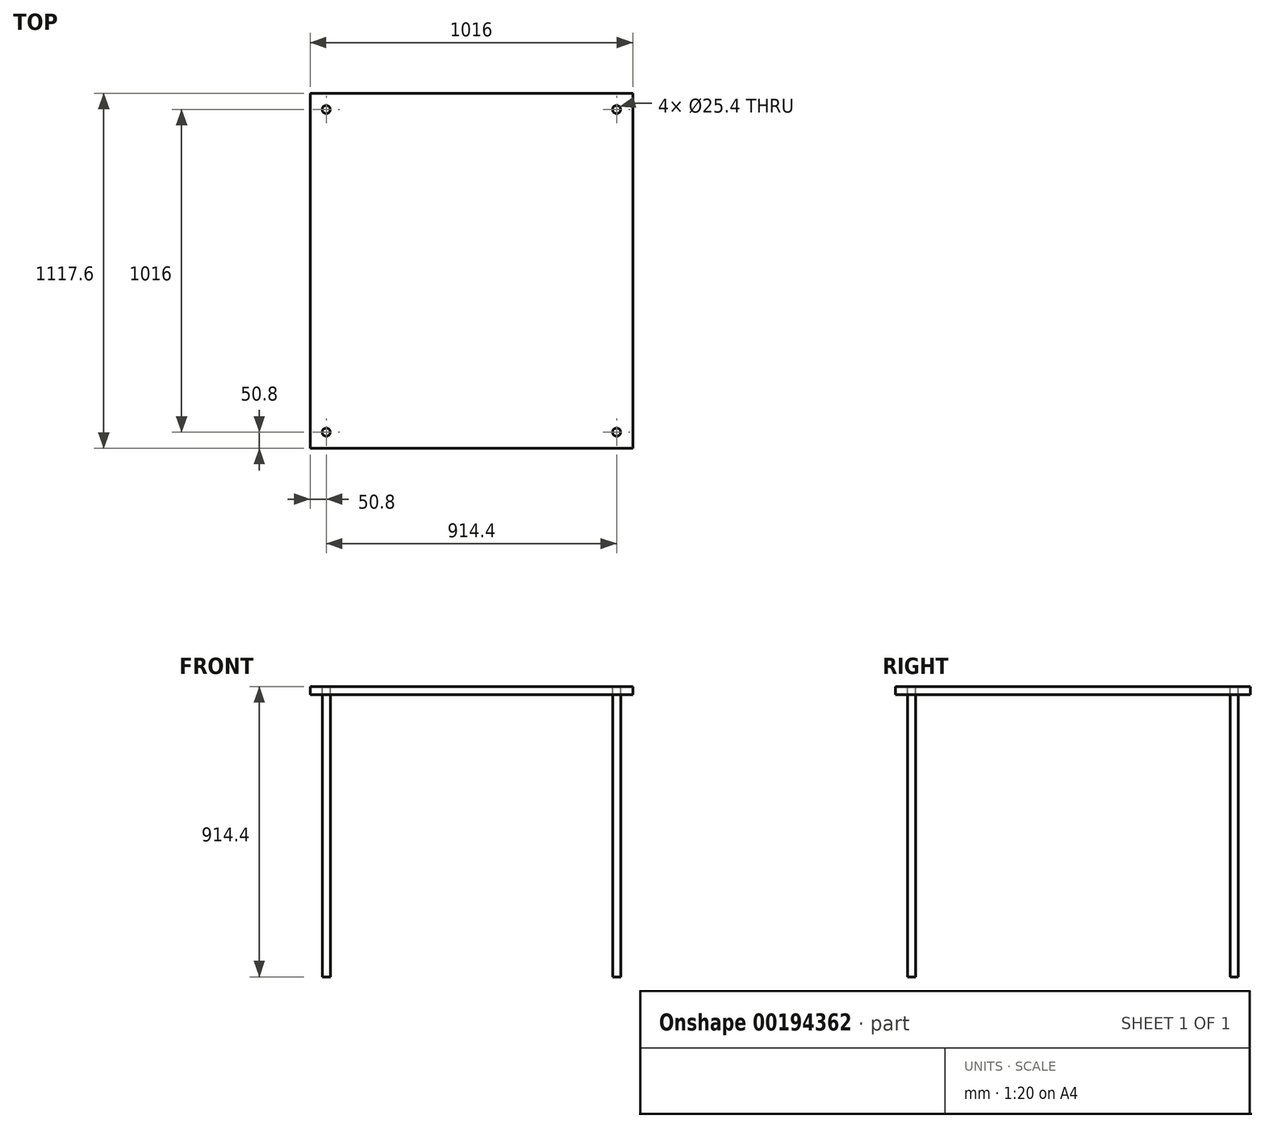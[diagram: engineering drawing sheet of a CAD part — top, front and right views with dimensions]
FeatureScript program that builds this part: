
annotation { "Feature Type Name" : "Feature", "Feature Type Description" : "" }
export const myFeature = defineFeature(function(context is Context, id is Id, definition is map)
    precondition{}
    {
        {
            var Q0;
            Q0=qCreatedBy(makeId("Top.planeOp"),FACE);
            var sketch = newSketch(context, id + "F0", { "sketchPlane" : qUnion([Q0])});
            skLineSegment(sketch, "E0.bottom", {"start": v(508, 558.8) * mm, "end": v(-508, 558.8) * mm});
            skLineSegment(sketch, "E0.top", {"start": v(508, -558.8) * mm, "end": v(-508, -558.8) * mm});
            skLineSegment(sketch, "E0.left", {"start": v(508, 558.8) * mm, "end": v(508, -558.8) * mm});
            skLineSegment(sketch, "E0.right", {"start": v(-508, 558.8) * mm, "end": v(-508, -558.8) * mm});
            skPoint(sketch, "E0.middle", {"position": v(0, 0) * mm});
            skLineSegment(sketch, "E1.bottom", {"start": v(457.2, 508) * mm, "end": v(-457.2, 508) * mm});
            skLineSegment(sketch, "E1.top", {"start": v(457.2, -508) * mm, "end": v(-457.2, -508) * mm});
            skLineSegment(sketch, "E1.left", {"start": v(457.2, 508) * mm, "end": v(457.2, -508) * mm});
            skLineSegment(sketch, "E1.right", {"start": v(-457.2, 508) * mm, "end": v(-457.2, -508) * mm});
            skCircle(sketch, "E2", {"center": v(-457.2, -508) * mm, "radius": 12.7 * mm});
            skCircle(sketch, "E3", {"center": v(457.2, -508) * mm, "radius": 12.7 * mm});
            skCircle(sketch, "E4", {"center": v(-457.2, 508) * mm, "radius": 12.7 * mm});
            skCircle(sketch, "E5", {"center": v(457.2, 508) * mm, "radius": 12.7 * mm});
            skSolve(sketch);
        }
        {
            var Q0;
            Q0=makeQuery(id+"F0.imprint","IMPRINT",FACE,{"disambiguationData":[TD([[makeQuery(id+"F0.imprint","IMPRINT",EDGE,{"derivedFrom":sQuery(id+"F0.wireOp",EDGE,"E0.bottom")}),1.0]])]});
            var Q1;
            {var subQ10=sQuery(id+"F0.wireOp",EDGE,"E5");var subQ13=sQuery(id+"F0.wireOp",EDGE,"E1.bottom");var subQ15=makeQuery(id+"F0.imprint","INTERSECT",VERTEX,{"derivedFrom":[subQ13,subQ10]});Q1=makeQuery(id+"F0.imprint","IMPRINT",FACE,{"disambiguationData":[TD([[makeQuery(id+"F0.imprint","IMPRINT",EDGE,{"disambiguationData":[TD([[subQ15,-1.0]])],"derivedFrom":subQ13}),1.0]])]});}
            extrude(context, id + "F1", {"entities" : qUnion([Q0, Q1]), "oppositeDirection" : true, "depth" : 25.4 * mm});
        }
        {
            var Q0;
            {var subQ0=sQuery(id+"F0.wireOp",EDGE,"E1.right");var subQ1=sQuery(id+"F0.wireOp",EDGE,"E1.top");var subQ2=makeQuery(id+"F0.imprint","INTERSECT",VERTEX,{"derivedFrom":[subQ1,subQ0]});Q0=makeQuery(id+"F0.imprint","IMPRINT",FACE,{"disambiguationData":[TD([[makeQuery(id+"F0.imprint","IMPRINT",EDGE,{"disambiguationData":[TD([[subQ2,1.0]])],"derivedFrom":subQ1}),1.0]])]});}
            var Q1;
            {var subQ0=sQuery(id+"F0.wireOp",EDGE,"E1.right");var subQ1=sQuery(id+"F0.wireOp",EDGE,"E1.top");var subQ2=makeQuery(id+"F0.imprint","INTERSECT",VERTEX,{"derivedFrom":[subQ1,subQ0]});Q1=makeQuery(id+"F0.imprint","IMPRINT",FACE,{"disambiguationData":[TD([[makeQuery(id+"F0.imprint","IMPRINT",EDGE,{"disambiguationData":[TD([[subQ2,1.0]])],"derivedFrom":subQ1}),-1.0]])]});}
            var Q2;
            {var subQ0=sQuery(id+"F0.wireOp",EDGE,"E1.left");var subQ1=sQuery(id+"F0.wireOp",EDGE,"E1.top");var subQ2=makeQuery(id+"F0.imprint","INTERSECT",VERTEX,{"derivedFrom":[subQ1,subQ0]});Q2=makeQuery(id+"F0.imprint","IMPRINT",FACE,{"disambiguationData":[TD([[makeQuery(id+"F0.imprint","IMPRINT",EDGE,{"disambiguationData":[TD([[subQ2,-1.0]])],"derivedFrom":subQ1}),1.0]])]});}
            var Q3;
            {var subQ0=sQuery(id+"F0.wireOp",EDGE,"E1.left");var subQ1=sQuery(id+"F0.wireOp",EDGE,"E1.top");var subQ2=makeQuery(id+"F0.imprint","INTERSECT",VERTEX,{"derivedFrom":[subQ1,subQ0]});Q3=makeQuery(id+"F0.imprint","IMPRINT",FACE,{"disambiguationData":[TD([[makeQuery(id+"F0.imprint","IMPRINT",EDGE,{"disambiguationData":[TD([[subQ2,-1.0]])],"derivedFrom":subQ1}),-1.0]])]});}
            var Q4;
            {var subQ0=sQuery(id+"F0.wireOp",EDGE,"E1.left");var subQ1=sQuery(id+"F0.wireOp",EDGE,"E1.bottom");var subQ2=makeQuery(id+"F0.imprint","INTERSECT",VERTEX,{"derivedFrom":[subQ1,subQ0]});Q4=makeQuery(id+"F0.imprint","IMPRINT",FACE,{"disambiguationData":[TD([[makeQuery(id+"F0.imprint","IMPRINT",EDGE,{"disambiguationData":[TD([[subQ2,-1.0]])],"derivedFrom":subQ1}),-1.0]])]});}
            var Q5;
            {var subQ0=sQuery(id+"F0.wireOp",EDGE,"E1.left");var subQ1=sQuery(id+"F0.wireOp",EDGE,"E1.bottom");var subQ2=makeQuery(id+"F0.imprint","INTERSECT",VERTEX,{"derivedFrom":[subQ1,subQ0]});Q5=makeQuery(id+"F0.imprint","IMPRINT",FACE,{"disambiguationData":[TD([[makeQuery(id+"F0.imprint","IMPRINT",EDGE,{"disambiguationData":[TD([[subQ2,-1.0]])],"derivedFrom":subQ1}),1.0]])]});}
            var Q6;
            {var subQ0=sQuery(id+"F0.wireOp",EDGE,"E1.right");var subQ1=sQuery(id+"F0.wireOp",EDGE,"E1.bottom");var subQ2=makeQuery(id+"F0.imprint","INTERSECT",VERTEX,{"derivedFrom":[subQ1,subQ0]});Q6=makeQuery(id+"F0.imprint","IMPRINT",FACE,{"disambiguationData":[TD([[makeQuery(id+"F0.imprint","IMPRINT",EDGE,{"disambiguationData":[TD([[subQ2,1.0]])],"derivedFrom":subQ1}),-1.0]])]});}
            var Q7;
            {var subQ0=sQuery(id+"F0.wireOp",EDGE,"E1.right");var subQ1=sQuery(id+"F0.wireOp",EDGE,"E1.bottom");var subQ2=makeQuery(id+"F0.imprint","INTERSECT",VERTEX,{"derivedFrom":[subQ1,subQ0]});Q7=makeQuery(id+"F0.imprint","IMPRINT",FACE,{"disambiguationData":[TD([[makeQuery(id+"F0.imprint","IMPRINT",EDGE,{"disambiguationData":[TD([[subQ2,1.0]])],"derivedFrom":subQ1}),1.0]])]});}
            extrude(context, id + "F2", {"entities" : qUnion([Q0, Q1, Q2, Q3, Q4, Q5, Q6, Q7]), "oppositeDirection" : true, "depth" : 914.4 * mm});
        }
    });
